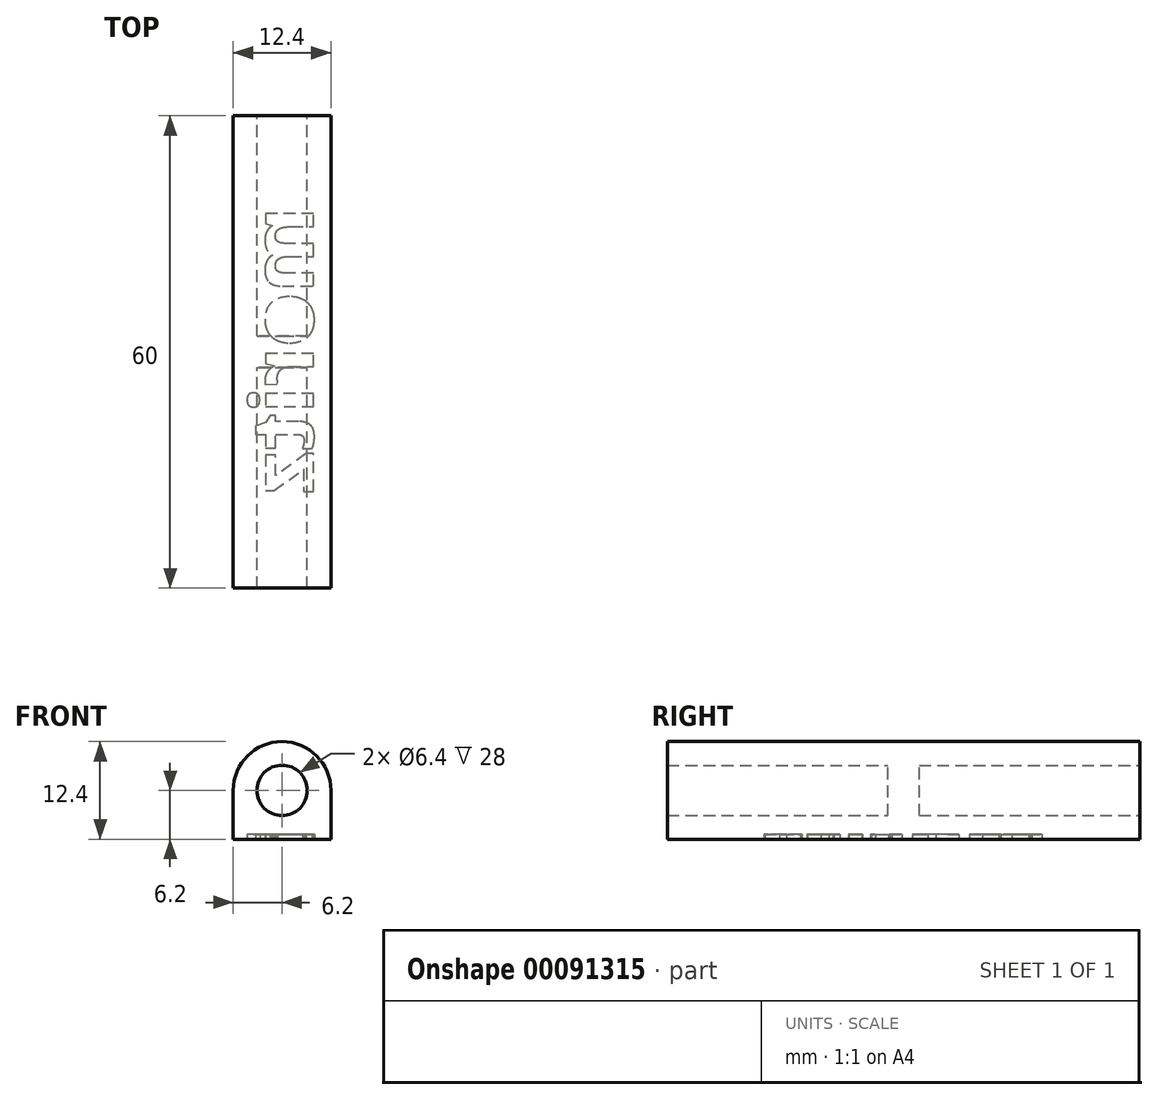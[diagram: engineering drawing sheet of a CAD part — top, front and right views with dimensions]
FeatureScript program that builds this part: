
annotation { "Feature Type Name" : "Feature", "Feature Type Description" : "" }
export const myFeature = defineFeature(function(context is Context, id is Id, definition is map)
    precondition{}
    {
        {
            var Q0;
            Q0=qCreatedBy(makeId("Front.planeOp"),FACE);
            var sketch = newSketch(context, id + "F0", { "sketchPlane" : qUnion([Q0])});
            skCircle(sketch, "E0", {"center": v(0, 0) * mm, "radius": 3.2 * mm});
            skCircle(sketch, "E1", {"center": v(0, 0) * mm, "radius": 6.2 * mm});
            skLineSegment(sketch, "E2", {"start": v(-6.2, 0) * mm, "end": v(-6.2, -6.2) * mm});
            skLineSegment(sketch, "E3", {"start": v(-6.2, -6.2) * mm, "end": v(6.2, -6.2) * mm});
            skLineSegment(sketch, "E4", {"start": v(6.2, -6.2) * mm, "end": v(6.2, 0) * mm});
            skSolve(sketch);
        }
        {
            var Q0;
            Q0 = qSketchRegion(id + "F0", true);
            extrude(context, id + "F1", {"entities" : qUnion([Q0]), "endBound" : BoundingType.SYMMETRIC, "depth" : 60 * mm, "offsetDistance" : 25 * mm});
        }
        {
            var Q0;
            Q0=makeQuery(id+"F1.opExtrude","SWEPT_FACE",FACE,{"disambiguationData":[OSD([sQuery(id+"F0.wireOp",EDGE,"E3")])]});
            var sketch = newSketch(context, id + "F2", { "sketchPlane" : qUnion([Q0])});
            skText(sketch, "E5", { "text": "moritz", "fontName": "OpenSans-Bold.ttf"});
            skPoint(sketch, "E6", {"position": v(0, 18.43) * mm});
            skPoint(sketch, "E7", {"position": v(0, 30) * mm});
            skPoint(sketch, "E8", {"position": v(6.2, 0) * mm});
            skLineSegment(sketch, "E9", {"start": v(4, -18.43) * mm, "end": v(4, 18.43) * mm});
            const initialGuessF2  = {"E5": [0.004, -0.01843, 0, 1, 0.008]};
            skSetInitialGuess(sketch, initialGuessF2);
            skSolve(sketch);
        }
        {
            var Q0;
            Q0=makeQuery(id+"F2.imprint","IMPRINT",FACE,{"disambiguationData":[TD([[makeQuery(id+"F2.imprint","IMPRINT",EDGE,{"derivedFrom":sQuery(id+"F2.wireOp",EDGE,"E5.sketch_text.stroke-46")}),-1.0]])]});
            var Q1;
            Q1=makeQuery(id+"F2.imprint","IMPRINT",FACE,{"disambiguationData":[TD([[makeQuery(id+"F2.imprint","IMPRINT",EDGE,{"derivedFrom":sQuery(id+"F2.wireOp",EDGE,"E5.sketch_text.stroke-59")}),-1.0]])]});
            var Q2;
            {var subQ0=sQuery(id+"F2.wireOp",EDGE,"E5.sketch_text.stroke-65");Q2=makeQuery(id+"F2.imprint","IMPRINT",FACE,{"disambiguationData":[TD([[makeQuery(id+"F2.imprint","IMPRINT",EDGE,{"derivedFrom":subQ0}),-1.0]])]});}
            var Q3;
            {var subQ0=sQuery(id+"F2.wireOp",EDGE,"E5.sketch_text.stroke-87");Q3=makeQuery(id+"F2.imprint","IMPRINT",FACE,{"disambiguationData":[TD([[makeQuery(id+"F2.imprint","IMPRINT",EDGE,{"derivedFrom":subQ0}),-1.0]])]});}
            var Q4;
            {var subQ0=sQuery(id+"F2.wireOp",EDGE,"E5.sketch_text.stroke-38");var subQ1=sQuery(id+"F2.wireOp",EDGE,"E5.sketch_text.stroke-37");var subQ2=makeQuery(id+"F2.imprint","INTERSECT",VERTEX,{"derivedFrom":[subQ1,subQ0]});Q4=makeQuery(id+"F2.imprint","IMPRINT",FACE,{"disambiguationData":[TD([[makeQuery(id+"F2.imprint","IMPRINT",EDGE,{"disambiguationData":[TD([[subQ2,1.0]])],"derivedFrom":subQ1}),-1.0]])]});}
            var Q5;
            Q5=makeQuery(id+"F2.imprint","IMPRINT",FACE,{"disambiguationData":[TD([[makeQuery(id+"F2.imprint","IMPRINT",EDGE,{"derivedFrom":sQuery(id+"F2.wireOp",EDGE,"E5.sketch_text.stroke-68")}),-1.0]])]});
            var Q6;
            {var subQ0=sQuery(id+"F2.wireOp",EDGE,"E5.sketch_text.stroke-71");var subQ1=sQuery(id+"F2.wireOp",EDGE,"E5.sketch_text.stroke-70");var subQ2=makeQuery(id+"F2.imprint","INTERSECT",VERTEX,{"derivedFrom":[subQ1,subQ0]});Q6=makeQuery(id+"F2.imprint","IMPRINT",FACE,{"disambiguationData":[TD([[makeQuery(id+"F2.imprint","IMPRINT",EDGE,{"disambiguationData":[TD([[subQ2,1.0]])],"derivedFrom":subQ1}),-1.0]])]});}
            var Q7;
            {var subQ3=sQuery(id+"F2.wireOp",EDGE,"E5.sketch_text.stroke-1");Q7=makeQuery(id+"F2.imprint","IMPRINT",FACE,{"disambiguationData":[TD([[makeQuery(id+"F2.imprint","IMPRINT",EDGE,{"derivedFrom":subQ3}),-1.0]])]});}
            var Q8;
            Q8=makeQuery(id+"F2.imprint","IMPRINT",FACE,{"disambiguationData":[TD([[makeQuery(id+"F2.imprint","IMPRINT",EDGE,{"derivedFrom":sQuery(id+"F2.wireOp",EDGE,"E5.sketch_text.stroke-28")}),-1.0]])]});
            var Q9;
            Q9=makeQuery(id+"F2.imprint","IMPRINT",FACE,{"disambiguationData":[TD([[makeQuery(id+"F2.imprint","IMPRINT",EDGE,{"derivedFrom":sQuery(id+"F2.wireOp",EDGE,"E5.sketch_text.stroke-28")}),1.0]])]});
            extrude(context, id + "F3", {"entities" : qUnion([Q0, Q1, Q2, Q3, Q4, Q5, Q6, Q7, Q8, Q9]), "operationType" : NewBodyOperationType.REMOVE, "oppositeDirection" : true, "depth" : 0.6 * mm, "offsetDistance" : 25 * mm});
        }
        {
            var Q0;
            Q0=qCreatedBy(makeId("Front.planeOp"),FACE);
            var sketch = newSketch(context, id + "F4", { "sketchPlane" : qUnion([Q0])});
            skCircle(sketch, "E10", {"center": v(0, 0) * mm, "radius": 3.2 * mm});
            skSolve(sketch);
        }
        {
            var Q0;
            Q0=makeQuery(id+"F4.imprint","IMPRINT",FACE,{"disambiguationData":[TD([[makeQuery(id+"F4.imprint","IMPRINT",EDGE,{"derivedFrom":sQuery(id+"F4.wireOp",EDGE,"E10")}),1.0]])]});
            extrude(context, id + "F5", {"entities" : qUnion([Q0]), "operationType" : NewBodyOperationType.ADD, "endBound" : BoundingType.SYMMETRIC, "depth" : 4 * mm, "offsetDistance" : 25 * mm});
        }
    });
